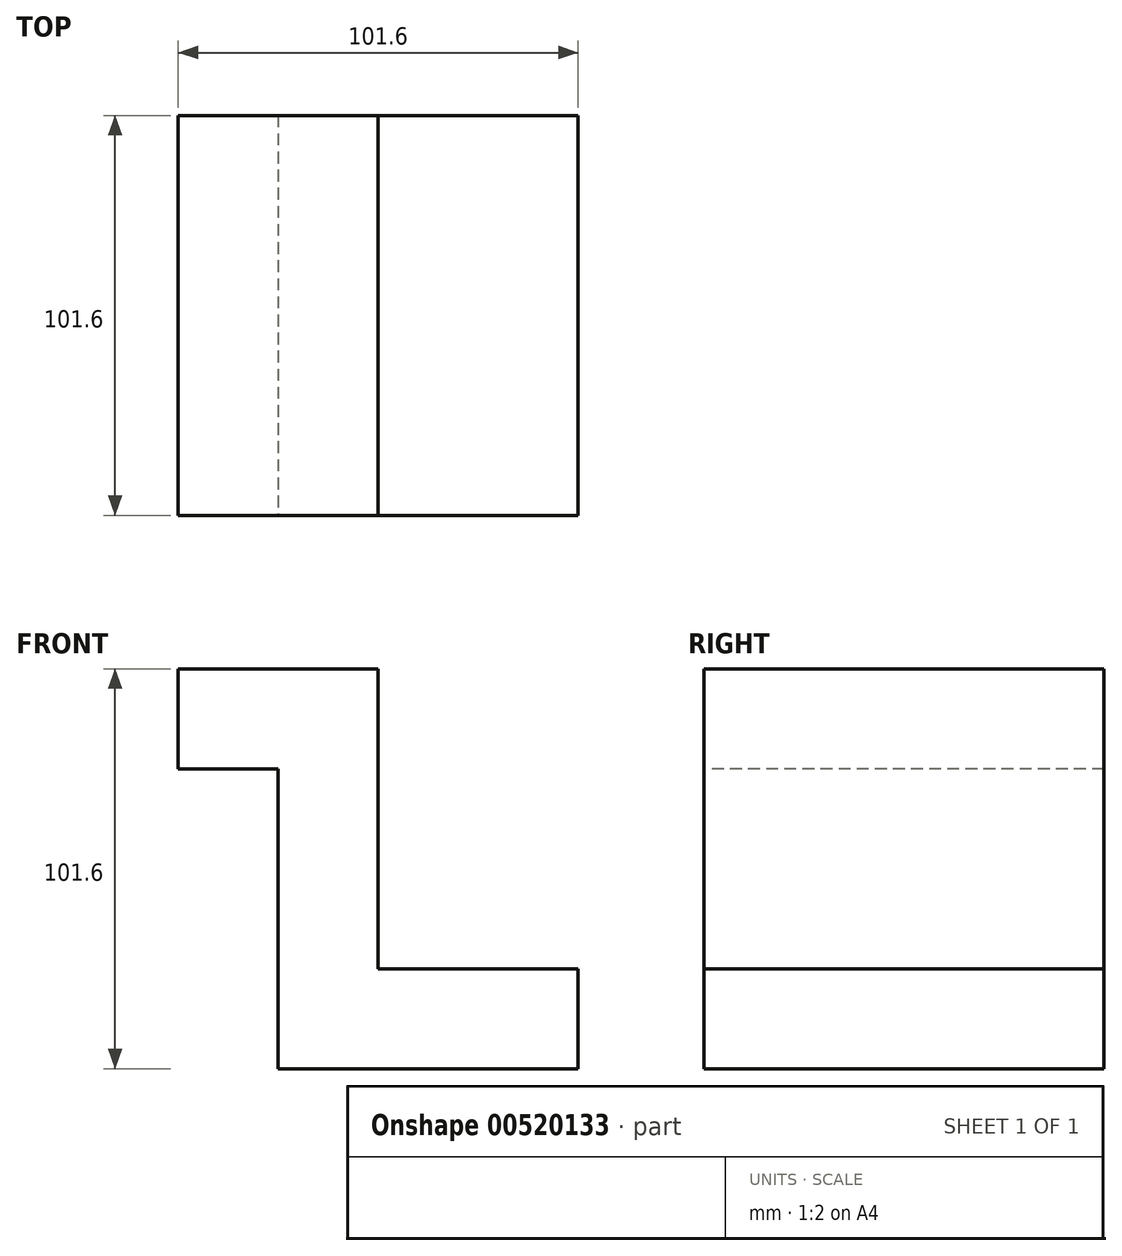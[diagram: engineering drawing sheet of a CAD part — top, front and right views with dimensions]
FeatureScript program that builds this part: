
annotation { "Feature Type Name" : "Feature", "Feature Type Description" : "" }
export const myFeature = defineFeature(function(context is Context, id is Id, definition is map)
    precondition{}
    {
        {
            var Q0;
            Q0=qCreatedBy(makeId("Top.planeOp"),FACE);
            var sketch = newSketch(context, id + "F0", { "sketchPlane" : qUnion([Q0])});
            skLineSegment(sketch, "E0.bottom", {"start": v(0, 0) * mm, "end": v(-101.6, 0) * mm});
            skLineSegment(sketch, "E0.top", {"start": v(0, -101.6) * mm, "end": v(-101.6, -101.6) * mm});
            skLineSegment(sketch, "E0.left", {"start": v(0, 0) * mm, "end": v(0, -101.6) * mm});
            skLineSegment(sketch, "E0.right", {"start": v(-101.6, 0) * mm, "end": v(-101.6, -101.6) * mm});
            skSolve(sketch);
        }
        {
            var Q0;
            Q0=makeQuery(id+"F0.imprint","IMPRINT",FACE,{"disambiguationData":[TD([[makeQuery(id+"F0.imprint","IMPRINT",EDGE,{"derivedFrom":sQuery(id+"F0.wireOp",EDGE,"E0.bottom")}),1.0]])]});
            extrude(context, id + "F1", {"entities" : qUnion([Q0]), "depth" : 101.6 * mm, "offsetDistance" : 25.4 * mm});
        }
        {
            var Q0;
            Q0=makeQuery(id+"F1.opExtrude","SWEPT_FACE",FACE,{"disambiguationData":[OSD([sQuery(id+"F0.wireOp",EDGE,"E0.top")])]});
            var sketch = newSketch(context, id + "F2", { "sketchPlane" : qUnion([Q0])});
            skLineSegment(sketch, "E1.bottom", {"start": v(-101.6, 0) * mm, "end": v(-76.2, 0) * mm});
            skLineSegment(sketch, "E1.top", {"start": v(-101.6, 76.2) * mm, "end": v(-76.2, 76.2) * mm});
            skLineSegment(sketch, "E1.left", {"start": v(-101.6, 0) * mm, "end": v(-101.6, 76.2) * mm});
            skLineSegment(sketch, "E1.right", {"start": v(-76.2, 0) * mm, "end": v(-76.2, 76.2) * mm});
            skLineSegment(sketch, "E2.bottom", {"start": v(0, 101.6) * mm, "end": v(-50.8, 101.6) * mm});
            skLineSegment(sketch, "E2.top", {"start": v(0, 25.4) * mm, "end": v(-50.8, 25.4) * mm});
            skLineSegment(sketch, "E2.left", {"start": v(0, 101.6) * mm, "end": v(0, 25.4) * mm});
            skLineSegment(sketch, "E2.right", {"start": v(-50.8, 101.6) * mm, "end": v(-50.8, 25.4) * mm});
            skSolve(sketch);
        }
        {
            var Q0;
            Q0=makeQuery(id+"F2.imprint","IMPRINT",FACE,{"disambiguationData":[TD([[makeQuery(id+"F2.imprint","IMPRINT",EDGE,{"derivedFrom":sQuery(id+"F2.wireOp",EDGE,"E1.bottom")}),-1.0]])]});
            var Q1;
            Q1=makeQuery(id+"F2.imprint","IMPRINT",FACE,{"disambiguationData":[TD([[makeQuery(id+"F2.imprint","IMPRINT",EDGE,{"derivedFrom":sQuery(id+"F2.wireOp",EDGE,"E2.bottom")}),1.0]])]});
            extrude(context, id + "F3", {"entities" : qUnion([Q0, Q1]), "operationType" : NewBodyOperationType.REMOVE, "oppositeDirection" : true, "depth" : 142.24 * mm, "offsetDistance" : 25.4 * mm});
        }
    });
